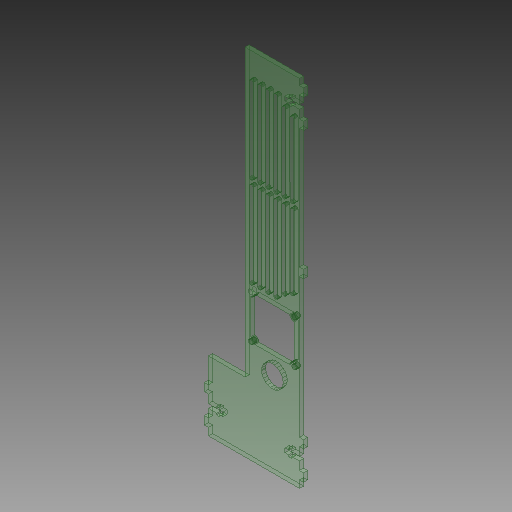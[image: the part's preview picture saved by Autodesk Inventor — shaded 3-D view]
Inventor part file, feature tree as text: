
AUTODESK INVENTOR PART (.ipt)
format: ipt  version: 2017 (Build 210142000, 142)  size: 742,912 bytes
history: native  units: mm
features: sketch x2, extrude x1, hole x1
ambient origin geometry x8: Origin, YZ Plane, XZ Plane, XY Plane, X Axis, Y Axis, Z Axis, Center Point
bodies: Solid1 (feature_tree)
feature tree (4):
  extrude  "Extrusion1"  [1 undecoded]
  hole  "Hole1"  [1 undecoded]
  sketch  "Sketch1"  dims[d0=3.0mm d1=0.0mm]
  sketch  "Sketch2"  dims[d2=3.4mm d3=6.0mm d4=4.0mm d5=2.0mm d6=90.0deg d7=8.0mm d8=20.594885mm]
note: 2 required parameter values undecoded (feature->parameter linkage not recoverable at this tier; creation-order binding heuristic only, values carry confidence <= 0.55)
